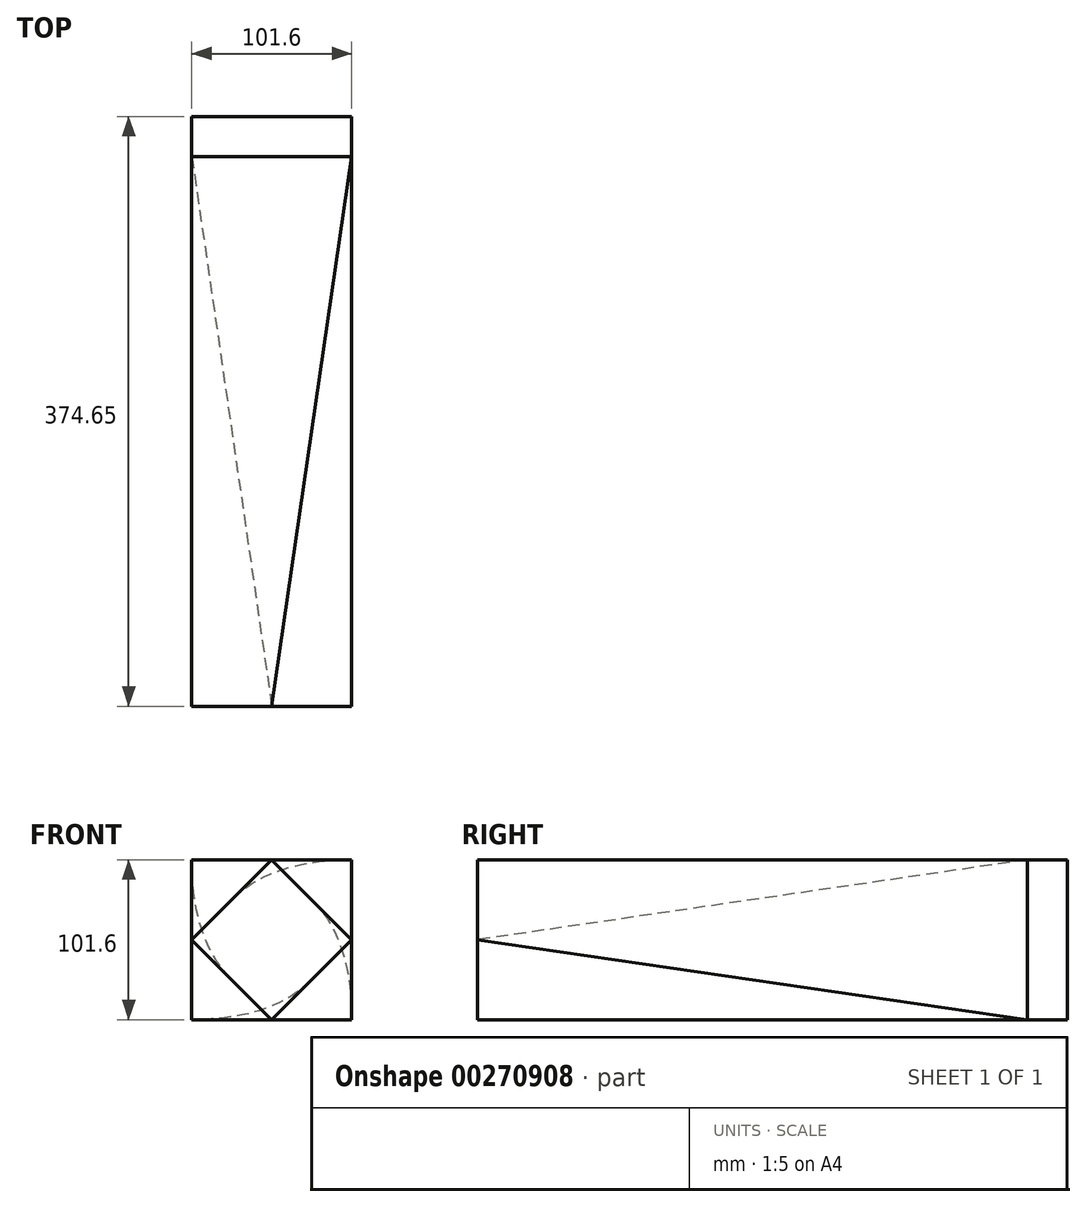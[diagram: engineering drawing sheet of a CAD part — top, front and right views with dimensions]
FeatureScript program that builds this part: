
annotation { "Feature Type Name" : "Feature", "Feature Type Description" : "" }
export const myFeature = defineFeature(function(context is Context, id is Id, definition is map)
    precondition{}
    {
        {
            var Q0;
            Q0=qCreatedBy(makeId("Front.planeOp"),FACE);
            var sketch = newSketch(context, id + "F0", { "sketchPlane" : qUnion([Q0])});
            skLineSegment(sketch, "E0.bottom", {"start": v(0, 0) * mm, "end": v(101.6, 0) * mm});
            skLineSegment(sketch, "E0.top", {"start": v(0, 101.6) * mm, "end": v(101.6, 101.6) * mm});
            skLineSegment(sketch, "E0.left", {"start": v(0, 0) * mm, "end": v(0, 101.6) * mm});
            skLineSegment(sketch, "E0.right", {"start": v(101.6, 0) * mm, "end": v(101.6, 101.6) * mm});
            skSolve(sketch);
        }
        {
            var Q0;
            Q0 = qSketchRegion(id + "F0", true);
            extrude(context, id + "F1", {"entities" : qUnion([Q0]), "depth" : 25.4 * mm});
        }
        {
            var Q0;
            Q0=makeQuery(id+"F1.opExtrude","CAP_FACE",FACE,{"disambiguationData":[OSD([sQuery(id+"F0.wireOp",EDGE,"E0.bottom"),sQuery(id+"F0.wireOp",EDGE,"E0.top"),sQuery(id+"F0.wireOp",EDGE,"E0.left"),sQuery(id+"F0.wireOp",EDGE,"E0.right")])],"isStart":false});
            cPlane(context, id + "F2", {"entities" : qUnion([Q0]), "cplaneType" : CPlaneType.OFFSET, "offset" : 349.25 * mm, "width" : 152.4 * mm, "height" : 152.4 * mm});
        }
        {
            var Q0;
            Q0=qCreatedBy(id+"F2.planeOp",FACE);
            var sketch = newSketch(context, id + "F3", { "sketchPlane" : qUnion([Q0])});
            skLineSegment(sketch, "E1", {"start": v(0, 50.8) * mm, "end": v(50.8, 101.6) * mm});
            skLineSegment(sketch, "E2", {"start": v(50.8, 101.6) * mm, "end": v(101.6, 50.8) * mm});
            skLineSegment(sketch, "E3", {"start": v(101.6, 50.8) * mm, "end": v(50.8, 0) * mm});
            skLineSegment(sketch, "E4", {"start": v(50.8, 0) * mm, "end": v(0, 50.8) * mm});
            skSolve(sketch);
        }
        {
            var Q1;
            Q1=makeQuery(id+"F1.opExtrude","CAP_FACE",FACE,{"disambiguationData":[OSD([sQuery(id+"F0.wireOp",EDGE,"E0.bottom"),sQuery(id+"F0.wireOp",EDGE,"E0.top"),sQuery(id+"F0.wireOp",EDGE,"E0.left"),sQuery(id+"F0.wireOp",EDGE,"E0.right")])],"isStart":false});
            var Q2;
            Q2=makeQuery(id+"F3.imprint","IMPRINT",FACE,{"disambiguationData":[TD([[makeQuery(id+"F3.imprint","IMPRINT",EDGE,{"derivedFrom":sQuery(id+"F3.wireOp",EDGE,"E1")}),-1.0]])]});
            loft(context, id + "F4", {"operationType" : NewBodyOperationType.ADD, "sheetProfilesArray" : [{ "sheetProfileEntities" : qUnion([Q1]) }, { "sheetProfileEntities" : qUnion([Q2]) }]});
        }
    });
